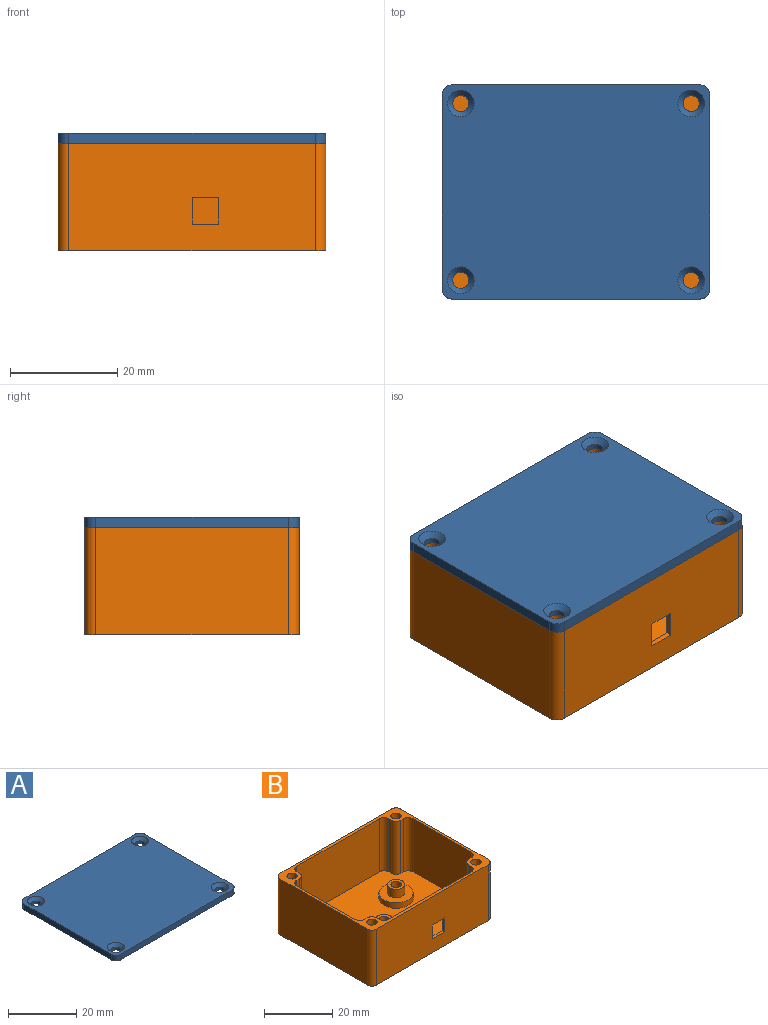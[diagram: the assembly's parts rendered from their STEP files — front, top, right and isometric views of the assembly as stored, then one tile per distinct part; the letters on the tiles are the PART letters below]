
ASSEMBLY  parts=2 mates=1
PART A: 18 faces, bbox 50x40x2 mm
  f0: plane 46x2mm, normal (0,1,0), area 92mm2, adj f4,f5,f14,f17
  f1: plane 36x2mm, normal (-1,0,0), area 72mm2, adj f4,f5,f14,f15
  f2: plane 46x2mm, normal (0,-1,0), area 92mm2, adj f4,f5,f15,f16
  f3: plane 36x2mm, normal (1,0,0), area 72mm2, adj f4,f5,f16,f17
  f4: plane 50x40mm, normal (0,0,1), area 1918mm2, adj f0,f1,f2,f3,f10,f11,f12,f13
  f5: plane 50x40mm, normal (0,0,-1), area 1968.3mm2, adj f0,f1,f2,f3,f6,f7,f8,f9
  f6: cylinder r=1.5mm len=3mm, axis (0,0,1), area 9.4mm2, adj f5,f13
  f7: cylinder r=1.5mm len=3mm, axis (0,0,1), area 9.4mm2, adj f5,f10
  f8: cylinder r=1.5mm len=3mm, axis (0,0,1), area 9.4mm2, adj f5,f12
  f9: cylinder r=1.5mm len=3mm, axis (0,0,1), area 9.4mm2, adj f5,f11
  f10: cone r=1.5mm half-angle=45deg, axis (0,0,1), area 17.8mm2, adj f4,f7
  f11: cone r=1.5mm half-angle=45deg, axis (0,0,1), area 17.8mm2, adj f4,f9
  f12: cone r=1.5mm half-angle=45deg, axis (0,0,1), area 17.8mm2, adj f4,f8
  f13: cone r=1.5mm half-angle=45deg, axis (0,0,1), area 17.8mm2, adj f4,f6
  f14: cylinder r=2mm len=2mm, axis (0,0,1), area 6.3mm2, adj f0,f1,f4,f5
  f15: cylinder r=2mm len=2mm, axis (0,0,-1), area 6.3mm2, adj f1,f2,f4,f5
  f16: cylinder r=2mm len=2mm, axis (0,0,1), area 6.3mm2, adj f2,f3,f4,f5
  f17: cylinder r=2mm len=2mm, axis (0,0,-1), area 6.3mm2, adj f0,f3,f4,f5
PART B: 71 faces, bbox 50x40x20 mm
  f0: plane 34x19mm, normal (0,1,0), area 621mm2, adj f4,f8,f55,f59,f67,f68,f69,f70
  f1: plane 46x20mm, normal (0,-1,0), area 895mm2, adj f8,f12,f52,f53,f67,f68,f69,f70
  f2: cylinder r=1.5mm len=4mm, axis (0,0,-1), area 37.7mm2, adj f30,f50
  f3: cylinder r=1.5mm len=4mm, axis (0,0,-1), area 37.7mm2, adj f32,f43
  f4: plane 48x38mm, normal (0,0,1), area 1563.5mm2, adj f0,f5,f6,f7,f13,f14,f15,f16
  f5: plane 24x19mm, normal (-1,0,0), area 456mm2, adj f4,f8,f57,f66
  f6: plane 24x19mm, normal (1,0,0), area 456mm2, adj f4,f8,f60,f61
  f7: plane 34x19mm, normal (0,-1,0), area 646mm2, adj f4,f8,f63,f65
  f8: plane 50x40mm, normal (0,0,1), area 247.7mm2, adj f0,f1,f5,f6,f7,f9,f10,f11
  f9: plane 46x20mm, normal (0,1,0), area 920mm2, adj f8,f12,f51,f54
  f10: plane 36x20mm, normal (-1,0,0), area 720mm2, adj f8,f12,f51,f52
  f11: plane 36x20mm, normal (1,0,0), area 720mm2, adj f8,f12,f53,f54
  f12: plane 50x40mm, normal (0,0,-1), area 1949.8mm2, adj f1,f9,f10,f11,f37,f38,f39,f40
  f13: plane 19x1mm, normal (0,-1,0), area 19mm2, adj f4,f8,f64,f66
  f14: plane 19x1mm, normal (-1,0,0), area 19mm2, adj f4,f8,f64,f65
  f15: plane 19x1mm, normal (0,-1,0), area 19mm2, adj f4,f8,f61,f62
  f16: plane 19x1mm, normal (1,0,0), area 19mm2, adj f4,f8,f62,f63
  f17: plane 19x1mm, normal (0,1,0), area 19mm2, adj f4,f8,f58,f60
  f18: plane 19x1mm, normal (1,0,0), area 19mm2, adj f4,f8,f58,f59
  f19: plane 19x1mm, normal (0,1,0), area 19mm2, adj f4,f8,f56,f57
  f20: plane 19x1mm, normal (-1,0,0), area 19mm2, adj f4,f8,f55,f56
  f21: cylinder r=1.5mm len=10mm, axis (0,0,1), area 94.2mm2, adj f8,f22
  f22: plane 3x3mm, normal (0,0,1), area 7.1mm2, adj f21
  f23: cylinder r=1.5mm len=10mm, axis (0,0,1), area 94.2mm2, adj f8,f24
  f24: plane 3x3mm, normal (0,0,1), area 7.1mm2, adj f23
  f25: cylinder r=1.5mm len=10mm, axis (0,0,1), area 94.2mm2, adj f8,f26
  f26: plane 3x3mm, normal (0,0,1), area 7.1mm2, adj f25
  f27: cylinder r=1.5mm len=10mm, axis (0,0,1), area 94.2mm2, adj f8,f28
  f28: plane 3x3mm, normal (0,0,1), area 7.1mm2, adj f27
  f29: cylinder r=2.5mm len=5mm, axis (0,0,-1), area 47.1mm2, adj f30,f34
  f30: plane 5x5mm, normal (0,0,1), area 12.6mm2, adj f2,f29
  f31: cylinder r=2.5mm len=5mm, axis (0,0,-1), area 47.1mm2, adj f32,f36
  f32: plane 5x5mm, normal (0,0,1), area 12.6mm2, adj f3,f31
  f33: cylinder r=5mm len=10mm, axis (0,0,-1), area 62.8mm2, adj f4,f34
  f34: plane 10x10mm, normal (0,0,1), area 58.9mm2, adj f29,f33
  f35: cylinder r=5mm len=10mm, axis (0,0,-1), area 62.8mm2, adj f4,f36
  f36: plane 10x10mm, normal (0,0,1), area 58.9mm2, adj f31,f35
  f37: plane 3x2mm, normal (1,0,0), area 6mm2, adj f12,f38,f42,f43
  f38: plane 2.6x2mm, normal (0.5,-0.87,0), area 6mm2, adj f12,f37,f39,f43
  f39: plane 2.6x2mm, normal (-0.5,-0.87,0), area 6mm2, adj f12,f38,f40,f43
  f40: plane 3x2mm, normal (-1,0,0), area 6mm2, adj f12,f39,f41,f43
  f41: plane 2.6x2mm, normal (-0.5,0.87,0), area 6mm2, adj f12,f40,f42,f43
  f42: plane 2.6x2mm, normal (0.5,0.87,0), area 6mm2, adj f12,f37,f41,f43
  f43: plane 6x5.2mm, normal (0,0,-1), area 16.3mm2, adj f3,f37,f38,f39,f40,f41,f42
  f44: plane 3x2mm, normal (1,0,0), area 6mm2, adj f12,f45,f49,f50
  f45: plane 2.6x2mm, normal (0.5,-0.87,0), area 6mm2, adj f12,f44,f46,f50
  f46: plane 2.6x2mm, normal (-0.5,-0.87,0), area 6mm2, adj f12,f45,f47,f50
  f47: plane 3x2mm, normal (-1,0,0), area 6mm2, adj f12,f46,f48,f50
  f48: plane 2.6x2mm, normal (-0.5,0.87,0), area 6mm2, adj f12,f47,f49,f50
  f49: plane 2.6x2mm, normal (0.5,0.87,0), area 6mm2, adj f12,f44,f48,f50
  f50: plane 6x5.2mm, normal (0,0,-1), area 16.3mm2, adj f2,f44,f45,f46,f47,f48,f49
  f51: cylinder r=2mm len=20mm, axis (0,0,1), area 62.8mm2, adj f8,f9,f10,f12
  f52: cylinder r=2mm len=20mm, axis (0,0,-1), area 62.8mm2, adj f1,f8,f10,f12
  f53: cylinder r=2mm len=20mm, axis (0,0,1), area 62.8mm2, adj f1,f8,f11,f12
  f54: cylinder r=2mm len=20mm, axis (0,0,-1), area 62.8mm2, adj f8,f9,f11,f12
  f55: cylinder r=2mm len=19mm, axis (0,0,1), area 59.7mm2, adj f0,f4,f8,f20
  f56: cylinder r=2mm len=19mm, axis (0,0,1), area 59.7mm2, adj f4,f8,f19,f20
  f57: cylinder r=2mm len=19mm, axis (0,0,1), area 59.7mm2, adj f4,f5,f8,f19
  f58: cylinder r=2mm len=19mm, axis (0,0,1), area 59.7mm2, adj f4,f8,f17,f18
  f59: cylinder r=2mm len=19mm, axis (0,0,-1), area 59.7mm2, adj f0,f4,f8,f18
  f60: cylinder r=2mm len=19mm, axis (0,0,1), area 59.7mm2, adj f4,f6,f8,f17
  f61: cylinder r=2mm len=19mm, axis (0,0,-1), area 59.7mm2, adj f4,f6,f8,f15
  f62: cylinder r=2mm len=19mm, axis (0,0,1), area 59.7mm2, adj f4,f8,f15,f16
  f63: cylinder r=2mm len=19mm, axis (0,0,-1), area 59.7mm2, adj f4,f7,f8,f16
  f64: cylinder r=2mm len=19mm, axis (0,0,1), area 59.7mm2, adj f4,f8,f13,f14
  f65: cylinder r=2mm len=19mm, axis (0,0,1), area 59.7mm2, adj f4,f7,f8,f14
  f66: cylinder r=2mm len=19mm, axis (0,0,-1), area 59.7mm2, adj f4,f5,f8,f13
  f67: plane 5x1mm, normal (0,0,-1), area 5mm2, adj f0,f1,f68,f70
  f68: plane 5x1mm, normal (1,0,0), area 5mm2, adj f0,f1,f67,f69
  f69: plane 5x1mm, normal (0,0,1), area 5mm2, adj f0,f1,f68,f70
  f70: plane 5x1mm, normal (-1,0,0), area 5mm2, adj f0,f1,f67,f69
PLACE A t=(-131.54,-24,39.88)mm
PLACE B t=(-51.62,-24.39,19.88)mm fixed
MATE slider B.f21 <-> A.f7  axis (0,0,1) through (-66.82,-7.04,39.88)mm
